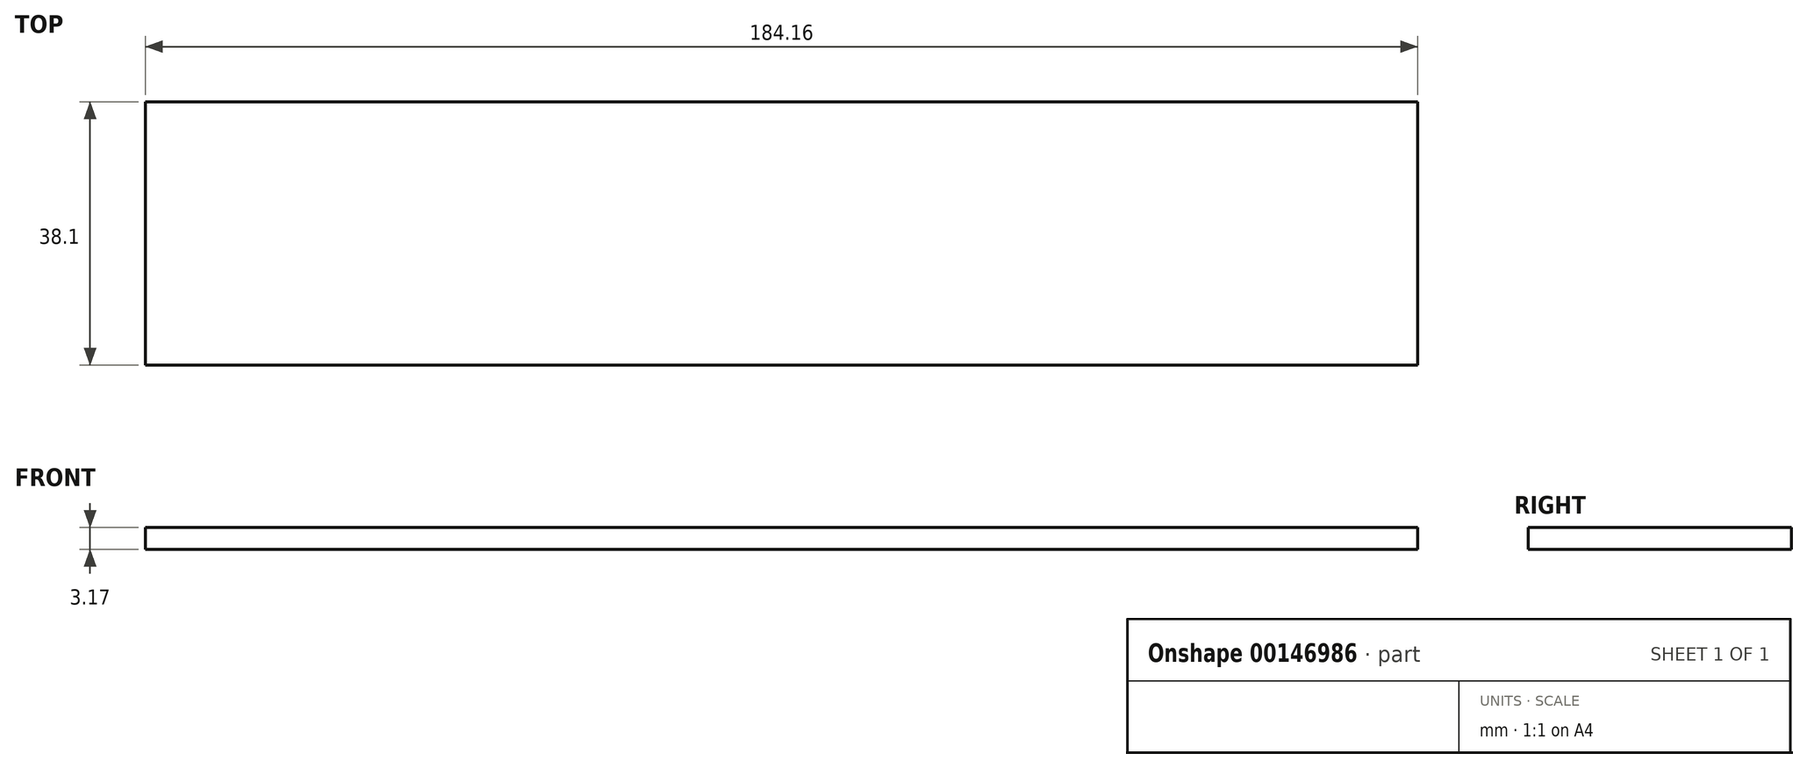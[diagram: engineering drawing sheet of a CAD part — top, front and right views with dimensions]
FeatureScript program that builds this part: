
annotation { "Feature Type Name" : "Feature", "Feature Type Description" : "" }
export const myFeature = defineFeature(function(context is Context, id is Id, definition is map)
    precondition{}
    {
        {
            var Q0;
            Q0=qCreatedBy(makeId("Top.planeOp"),FACE);
            var sketch = newSketch(context, id + "F0", { "sketchPlane" : qUnion([Q0])});
            skLineSegment(sketch, "E0.bottom", {"start": v(92.08, 19.05) * mm, "end": v(-92.08, 19.05) * mm});
            skLineSegment(sketch, "E0.top", {"start": v(92.08, -19.05) * mm, "end": v(-92.08, -19.05) * mm});
            skLineSegment(sketch, "E0.left", {"start": v(92.08, 19.05) * mm, "end": v(92.08, -19.05) * mm});
            skLineSegment(sketch, "E0.right", {"start": v(-92.08, 19.05) * mm, "end": v(-92.08, -19.05) * mm});
            skPoint(sketch, "E0.middle", {"position": v(0, 0) * mm});
            skSolve(sketch);
        }
        {
            var Q0;
            Q0 = qSketchRegion(id + "F0", true);
            extrude(context, id + "F1", {"entities" : qUnion([Q0]), "depth" : 3.17 * mm});
        }
    });
